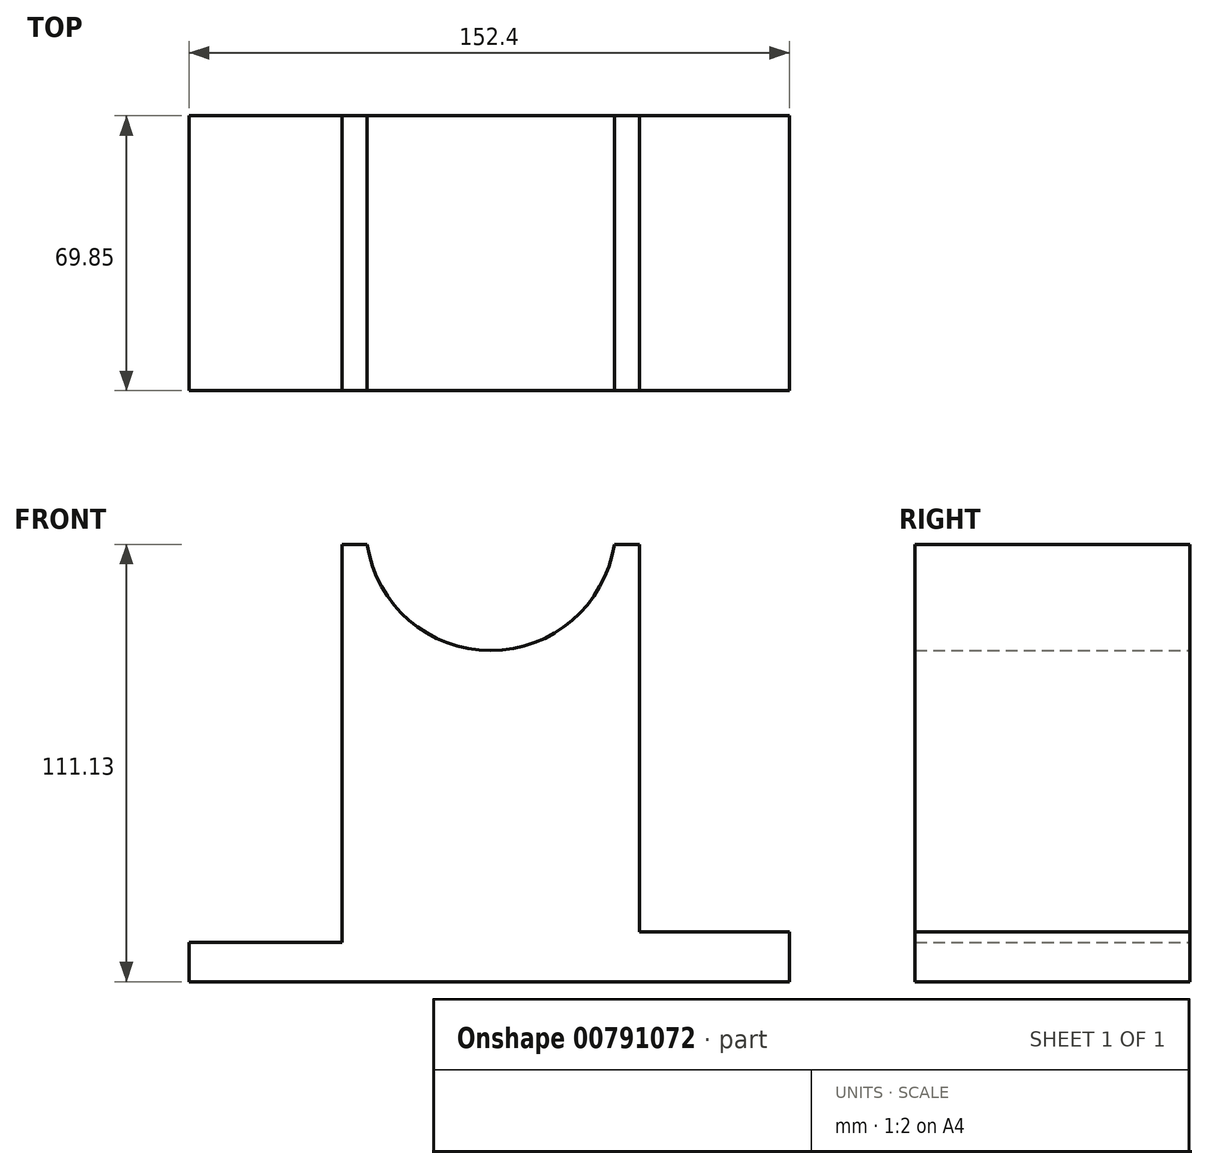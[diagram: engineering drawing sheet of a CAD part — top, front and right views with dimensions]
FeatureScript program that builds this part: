
annotation { "Feature Type Name" : "Feature", "Feature Type Description" : "" }
export const myFeature = defineFeature(function(context is Context, id is Id, definition is map)
    precondition{}
    {
        {
            var Q0;
            Q0=qCreatedBy(makeId("Front.planeOp"),FACE);
            var sketch = newSketch(context, id + "F0", { "sketchPlane" : qUnion([Q0])});
            skLineSegment(sketch, "E0", {"start": v(0, 0) * mm, "end": v(152.4, 0) * mm});
            skLineSegment(sketch, "E1", {"start": v(152.4, 0) * mm, "end": v(152.4, 12.7) * mm});
            skLineSegment(sketch, "E2", {"start": v(152.4, 12.7) * mm, "end": v(114.3, 12.7) * mm});
            skLineSegment(sketch, "E3", {"start": v(114.3, 12.7) * mm, "end": v(114.3, 111.12) * mm});
            skLineSegment(sketch, "E4", {"start": v(114.3, 111.12) * mm, "end": v(107.95, 111.12) * mm});
            skArc(sketch, "E5", {"start": v(45.16, 111.13) * mm, "mid": v(76.56, 84.12) * mm, "end": v(107.95, 111.12) * mm});
            skLineSegment(sketch, "E6", {"start": v(45.16, 111.13) * mm, "end": v(38.81, 111.13) * mm});
            skLineSegment(sketch, "E7", {"start": v(38.81, 111.13) * mm, "end": v(38.81, 9.97) * mm});
            skLineSegment(sketch, "E8", {"start": v(38.81, 9.97) * mm, "end": v(0, 9.97) * mm});
            skLineSegment(sketch, "E9", {"start": v(0, 9.97) * mm, "end": v(0, 0) * mm});
            skSolve(sketch);
        }
        {
            var Q0;
            Q0 = qSketchRegion(id + "F0", true);
            extrude(context, id + "F1", {"entities" : qUnion([Q0]), "depth" : 69.85 * mm, "offsetDistance" : 25.4 * mm});
        }
    });
